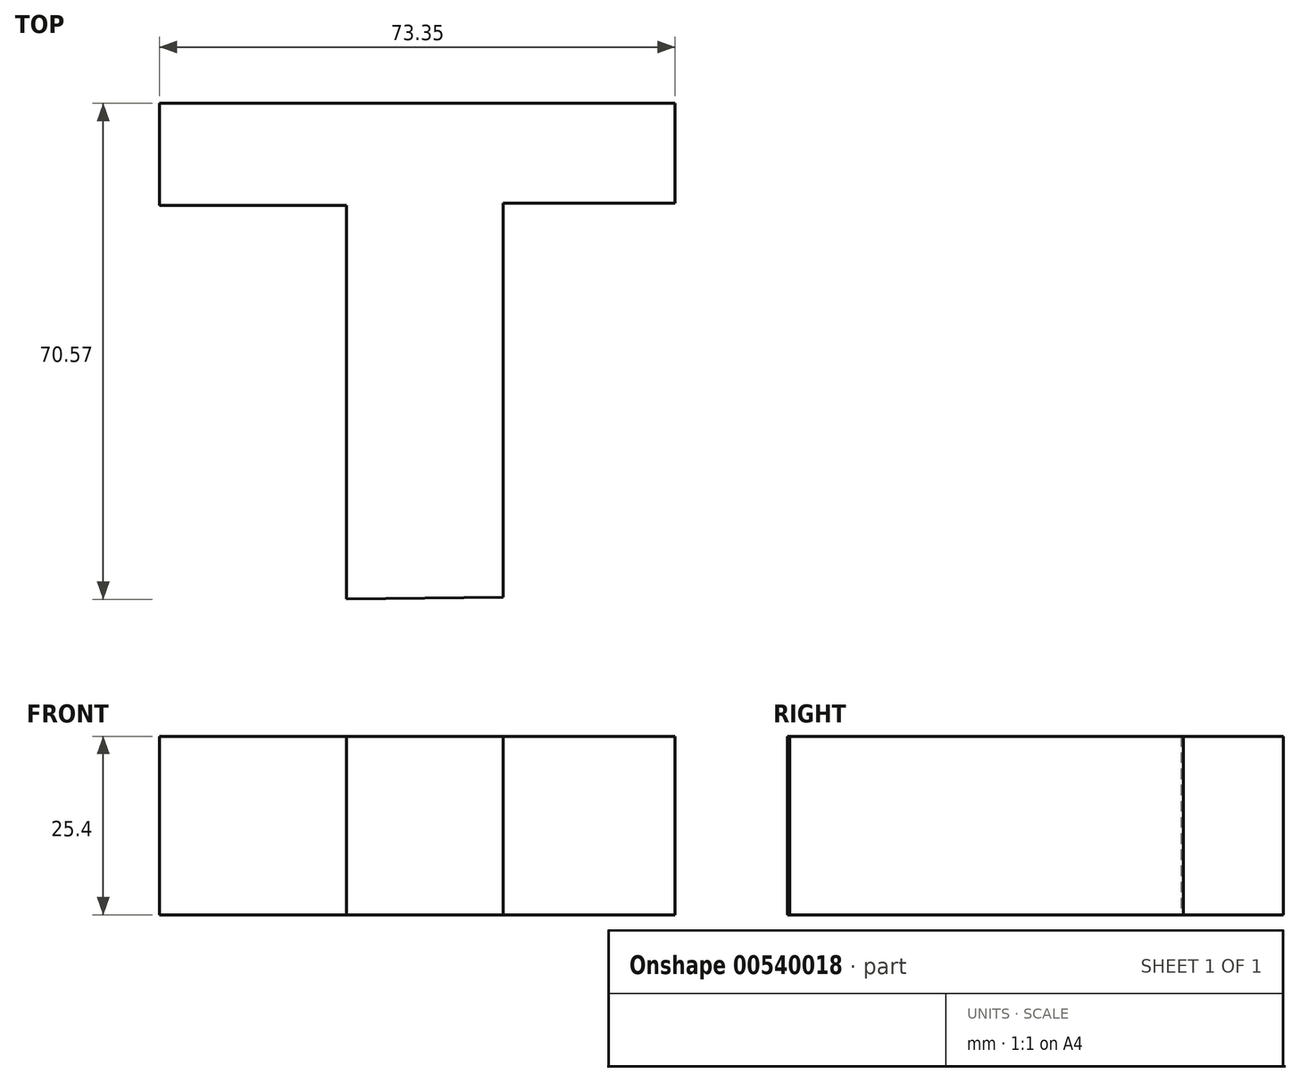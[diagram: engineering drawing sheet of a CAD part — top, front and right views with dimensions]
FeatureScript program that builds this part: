
annotation { "Feature Type Name" : "Feature", "Feature Type Description" : "" }
export const myFeature = defineFeature(function(context is Context, id is Id, definition is map)
    precondition{}
    {
        {
            var Q0;
            Q0=qCreatedBy(makeId("Top.planeOp"),FACE);
            var sketch = newSketch(context, id + "F0", { "sketchPlane" : qUnion([Q0])});
            skLineSegment(sketch, "E0", {"start": v(-35.28, 33.9) * mm, "end": v(38.07, 33.9) * mm});
            skLineSegment(sketch, "E1", {"start": v(-35.28, 33.9) * mm, "end": v(-35.28, 19.34) * mm});
            skLineSegment(sketch, "E2", {"start": v(38.07, 33.9) * mm, "end": v(38.07, 19.65) * mm});
            skLineSegment(sketch, "E3", {"start": v(-35.28, 19.34) * mm, "end": v(-8.67, 19.34) * mm});
            skLineSegment(sketch, "E4", {"start": v(38.07, 19.65) * mm, "end": v(13.62, 19.65) * mm});
            skLineSegment(sketch, "E5", {"start": v(13.62, 19.65) * mm, "end": v(13.62, -36.37) * mm});
            skLineSegment(sketch, "E6", {"start": v(-8.67, 19.34) * mm, "end": v(-8.67, -36.68) * mm});
            skLineSegment(sketch, "E7", {"start": v(-8.67, -36.68) * mm, "end": v(13.62, -36.37) * mm});
            skSolve(sketch);
        }
        {
            var Q0;
            Q0=makeQuery(id+"F0.imprint","IMPRINT",FACE,{"disambiguationData":[TD([[makeQuery(id+"F0.imprint","IMPRINT",EDGE,{"derivedFrom":sQuery(id+"F0.wireOp",EDGE,"E0")}),-1.0]])]});
            extrude(context, id + "F1", {"entities" : qUnion([Q0]), "depth" : 25.4 * mm, "offsetDistance" : 25.4 * mm});
        }
    });
